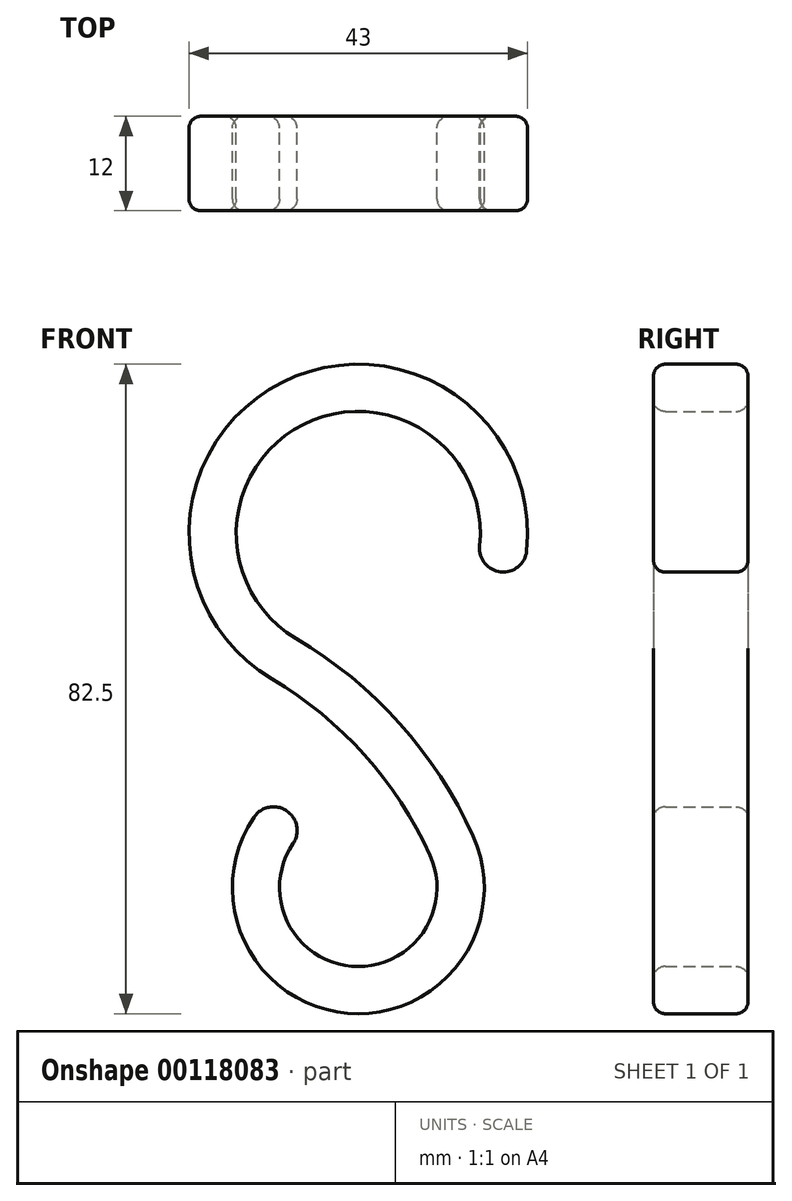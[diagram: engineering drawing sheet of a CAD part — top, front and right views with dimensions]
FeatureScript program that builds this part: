
annotation { "Feature Type Name" : "Feature", "Feature Type Description" : "" }
export const myFeature = defineFeature(function(context is Context, id is Id, definition is map)
    precondition{}
    {
        {
            var Q0;
            Q0=qCreatedBy(makeId("Front.planeOp"),FACE);
            var sketch = newSketch(context, id + "F0", { "sketchPlane" : qUnion([Q0])});
            skArc(sketch, "E0", {"start": v(15.42, -1.6) * mm, "mid": v(-6.97, 13.84) * mm, "end": v(-7.9, -13.34) * mm});
            skArc(sketch, "E1", {"start": v(21.39, -2.21) * mm, "mid": v(-9.67, 19.2) * mm, "end": v(-10.95, -18.5) * mm});
            skArc(sketch, "E2", {"start": v(-8.28, -39.4) * mm, "mid": v(-0.84, -54.96) * mm, "end": v(9.1, -40.87) * mm});
            skArc(sketch, "E3", {"start": v(-13.26, -36.04) * mm, "mid": v(-1.35, -60.94) * mm, "end": v(14.57, -38.39) * mm});
            skArc(sketch, "E4", {"start": v(9.1, -40.87) * mm, "mid": v(0.8, -28.14) * mm, "end": v(-10.95, -18.5) * mm});
            skArc(sketch, "E5", {"start": v(14.57, -38.39) * mm, "mid": v(5.26, -24.14) * mm, "end": v(-7.9, -13.34) * mm});
            skArc(sketch, "E6", {"start": v(-8.28, -39.4) * mm, "mid": v(-9.09, -35.23) * mm, "end": v(-13.26, -36.04) * mm});
            skArc(sketch, "E7", {"start": v(15.42, -1.6) * mm, "mid": v(18.1, -4.89) * mm, "end": v(21.39, -2.21) * mm});
            skSolve(sketch);
        }
        {
            var Q0;
            Q0=makeQuery(id+"F0.imprint","IMPRINT",FACE,{"disambiguationData":[TD([[makeQuery(id+"F0.imprint","IMPRINT",EDGE,{"derivedFrom":sQuery(id+"F0.wireOp",EDGE,"E0")}),-1.0]])]});
            extrude(context, id + "F1", {"entities" : qUnion([Q0]), "offsetDistance" : 25 * mm, "depth" : 12 * mm});
        }
        {
            var Q0;
            Q0=makeQuery(id+"F1.opExtrude","CAP_EDGE",EDGE,{"disambiguationData":[OSD([sQuery(id+"F0.wireOp",EDGE,"E1")])],"isStart":false});
            var Q1;
            Q1=makeQuery(id+"F1.opExtrude","CAP_EDGE",EDGE,{"disambiguationData":[OSD([sQuery(id+"F0.wireOp",EDGE,"E1")])],"isStart":true});
            fillet(context, id + "F2", {"entities" : qUnion([Q0, Q1]), "radius" : 1.5 * mm, "tangentPropagation" : true, "allowEdgeOverflow" : false});
        }
    });
